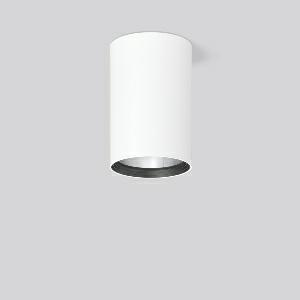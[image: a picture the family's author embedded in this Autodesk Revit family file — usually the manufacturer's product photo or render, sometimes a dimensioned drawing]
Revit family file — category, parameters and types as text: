
# Revit family: heledon_maxi_a_931223_002_2_4884
name_source: partatom
category: Lighting Fixtures
units: mm (PartAtom-declared; Revit-internal decimal feet)

## family parameters
Cut with Voids When Loaded = No
Host = Face
Light Source = No
Part Type = Normal
Room Calculation Point = No
Round Connector Dimension = Use Diameter
Shared = No

## types (1)
- HELEDON maxi A (1 x LED Modul 927, 4000 lm, 2700)
    Apparent Load = 35 VA
    Approval mark = CE
    CIE Flux Codes = 100 100 100 100 100
    Color Rendering = 92
    Color Temperature = 2700
    Default Elevation = 1800 mm
    Description = Series: HELEDON maxi
Cylindrical surface-mounted downlight. Housing: die-cast aluminium, powder-coated. Internal ceiling frame polycarbonate with bayonet mounting. Black plastic ring and recessed LED to prevent glare from the side. Optical assembly with reflector made of MIRO-Silver with 98% total light reflection for outstanding efficiency - can be changed without tools. Best colour rendering index Ra>90. Suitable for Ceiling mounting. Easy installation with a separate ceiling frame with bayonet mounting and plug connection. Driver integrated. Connected via plug-in connector. High quality converter without flickering and stroboscopic effect. The following accessories can be mounted without use of tools: interchangeable lenses, decorative glasses, honeycomb louvre, clear and frosted diffusers, white interchangeable plastic ring. 
Colour: traffic white, matt (RAL 9016)
Diameter: 123 mm
Height: 183 mm
Lamp: LED
Socket: without socket
Colour temperature: 2700K
Colour rendering index (CRI): 92
System power: 35 W
Rated luminous flux: 4000 lm
Luminous efficiency: 114 lm/W
Control gear: Regulated power supply
Protection class: I
Type of protection: IP 20
    Height = 183 mm
    Lamp = 1 x LED Modul 927
    Lamp Light Flux = 4000 lm
    Lamp count = 1
    Length = 123 mm
    Lifetime = 50000 h
    Luminous efficacy = 114 lm/W
    Manufacturer = RZB
    ModVariant = No
    Model = 931223.002.2
    Mounting Place = Ceiling
    Mounting Type = Surface mounted
    Number of Poles = 1
    OnlyDefault = Yes
    Power Factor = 1
    Product Name = HELEDON maxi A
    Product group = Surface mounted downlights
    ProductGroupID = 302
    Protection Class = Protection class I
    Protection Degree = IP 20
    RLX_Detail_Level = 1
    RLX_Emergency_Light_Flux = 0 lm
    RLX_Emergency_Type = 0
    RLX_Emergency_Type_DB = No
    RlxData = <blob elided: 96933 chars, md5=7c1f4076>
    Socket = socket
    Standby Power = 0 W
    System Light Flux = 4000 lm
    System Power = 35 W
    Type Comments = Product without accessories
    Type Image = 931192.002.jpg
    URL = http://relux.com
    VarID = ---
    Voltage = 230 V
    Voltage Range = 220-240 V
    Weight = 0.00 kg
    Width = 0 mm  [stored 0 ft]

note: [stored X ft] marks values corroborated as IEEE doubles in the binary element streams (Revit-internal decimal feet)

## geometry (parser evidence)
native form markers: Blend x4, Sweep x11
no freeform markers — native parametric forms only
